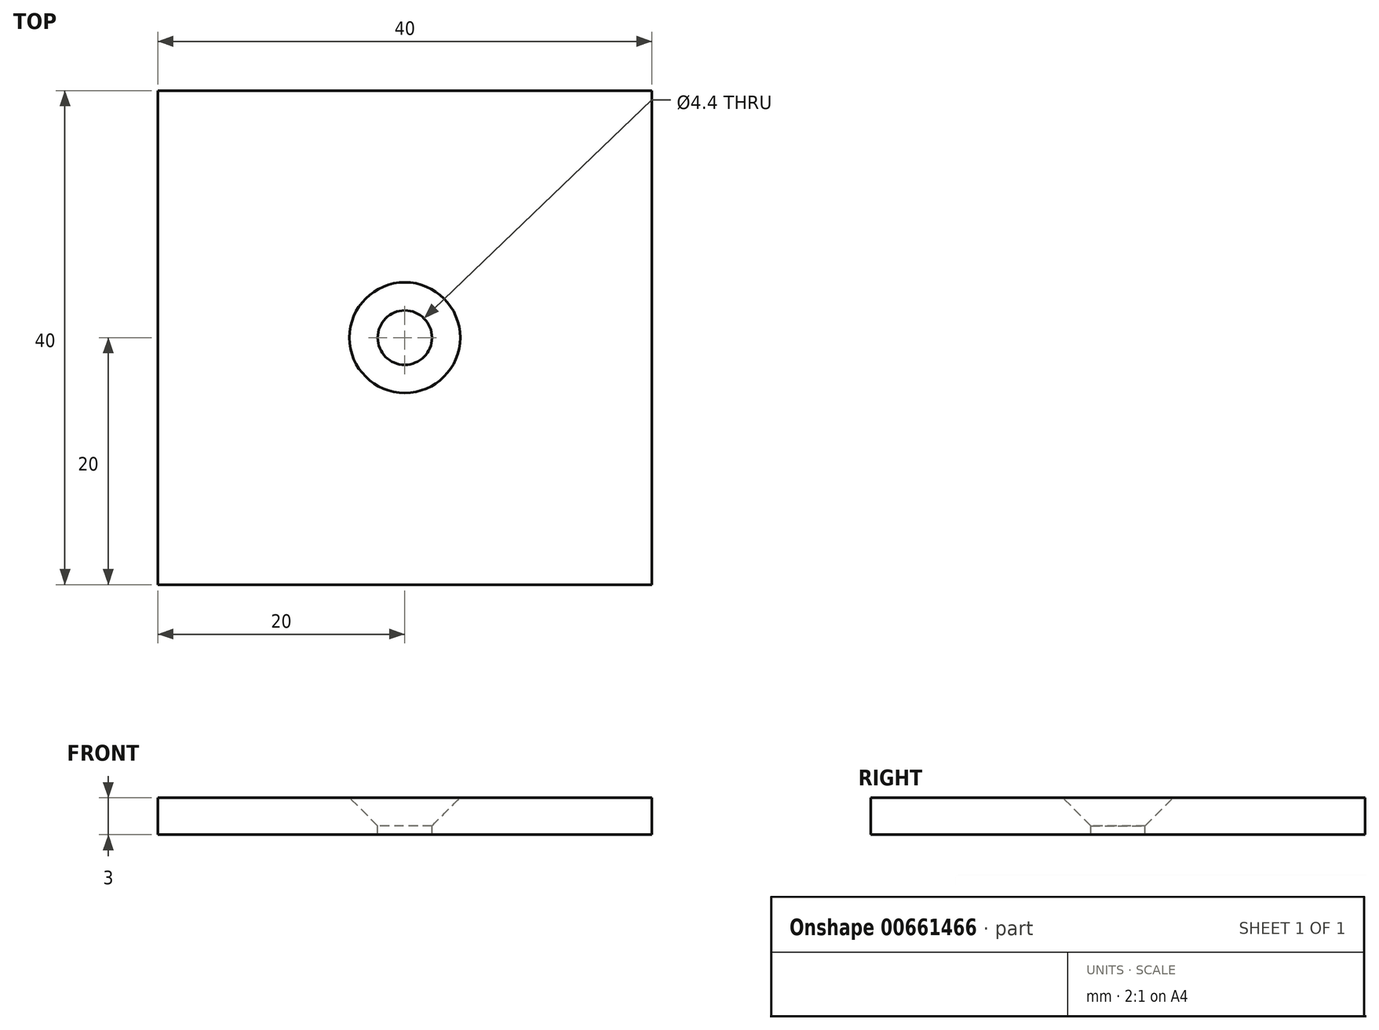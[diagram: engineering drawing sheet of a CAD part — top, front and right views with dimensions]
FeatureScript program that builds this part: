
annotation { "Feature Type Name" : "Feature", "Feature Type Description" : "" }
export const myFeature = defineFeature(function(context is Context, id is Id, definition is map)
    precondition{}
    {
        {
            var Q0;
            Q0=qCreatedBy(makeId("Top.planeOp"),FACE);
            var sketch = newSketch(context, id + "F0", { "sketchPlane" : qUnion([Q0])});
            skLineSegment(sketch, "E0.bottom", {"start": v(-20, 20) * mm, "end": v(20, 20) * mm});
            skLineSegment(sketch, "E0.top", {"start": v(-20, -20) * mm, "end": v(20, -20) * mm});
            skLineSegment(sketch, "E0.left", {"start": v(-20, 20) * mm, "end": v(-20, -20) * mm});
            skLineSegment(sketch, "E0.right", {"start": v(20, 20) * mm, "end": v(20, -20) * mm});
            skPoint(sketch, "E0.middle", {"position": v(0, 0) * mm});
            skSolve(sketch);
        }
        {
            var Q0;
            Q0 = qSketchRegion(id + "F0", true);
            extrude(context, id + "F1", {"entities" : qUnion([Q0]), "depth" : 3 * mm, "offsetDistance" : 25 * mm});
        }
        {
            var Q0;
            Q0=makeQuery(id+"F1.opExtrude","CAP_FACE",FACE,{"disambiguationData":[OSD([sQuery(id+"F0.wireOp",EDGE,"E0.bottom"),sQuery(id+"F0.wireOp",EDGE,"E0.top"),sQuery(id+"F0.wireOp",EDGE,"E0.left"),sQuery(id+"F0.wireOp",EDGE,"E0.right")])],"isStart":false});
            var sketch = newSketch(context, id + "F2", { "sketchPlane" : qUnion([Q0])});
            skPoint(sketch, "E1", {"position": v(0, 0) * mm});
            skSolve(sketch);
        }
        {
            var Q0;
            Q0=sQuery(id+"F2.wireOp",VERTEX,"E1");
            var Q1;
            Q1=makeQuery(id+"F1.opExtrude","SWEPT_BODY",BODY,{"disambiguationData":[OSD([sQuery(id+"F0.wireOp",EDGE,"E0.bottom"),sQuery(id+"F0.wireOp",EDGE,"E0.top"),sQuery(id+"F0.wireOp",EDGE,"E0.left"),sQuery(id+"F0.wireOp",EDGE,"E0.right")])]});
            hole(context, id + "F3", {"style" : HoleStyle.C_SINK, "endStyle" : HoleEndStyle.THROUGH, "standardTappedOrClearance" : lookupTablePath({ "standard" : "ISO", "fit" : "Normal", "size" : "M4", "type" : "Clearance" }), "standardBlindInLast" : lookupTablePath({ "fit" : "Standard", "standard" : "ISO", "size" : "M4", "type" : "Clearance" }), "holeDiameter" : 4.4 * mm, "cSinkDiameter" : 8.96 * mm, "cSinkAngle" : 90 * degree, "majorDiameter" : 5 * mm, "isTappedThrough" : true, "tappedDepth" : 12 * mm, "tapClearance" : 3, "startFromSketch" : true, "locations" : qUnion([Q0]), "scope" : qUnion([Q1])});
        }
    });
